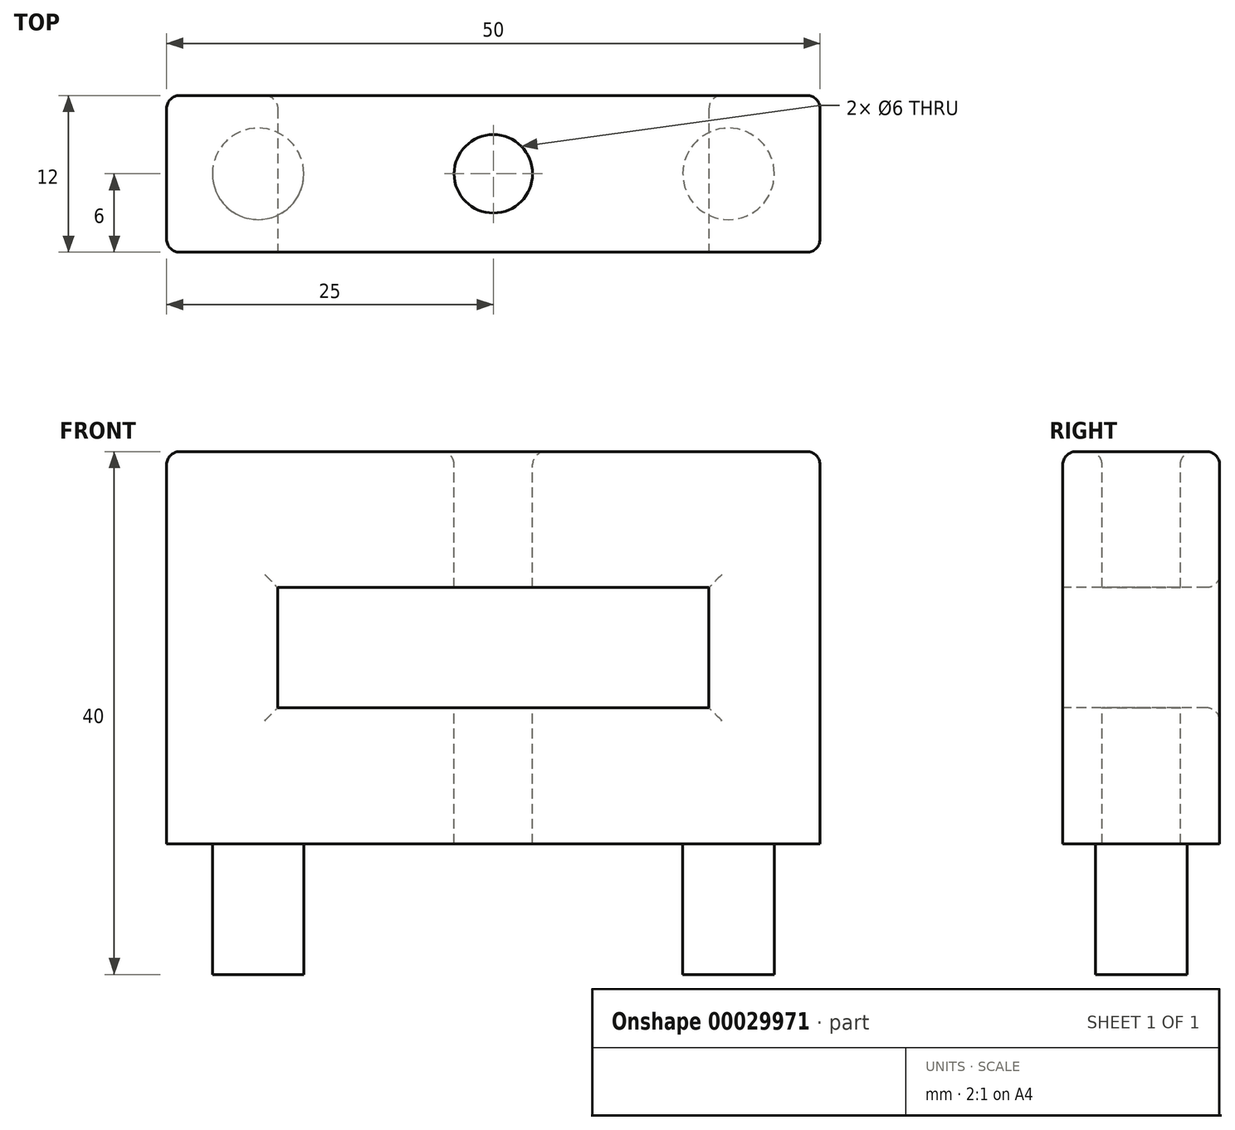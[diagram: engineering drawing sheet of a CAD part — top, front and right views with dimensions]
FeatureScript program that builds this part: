
annotation { "Feature Type Name" : "Feature", "Feature Type Description" : "" }
export const myFeature = defineFeature(function(context is Context, id is Id, definition is map)
    precondition{}
    {
        {
            var Q0;
            Q0=qCreatedBy(makeId("Top.planeOp"),FACE);
            var sketch = newSketch(context, id + "F0", { "sketchPlane" : qUnion([Q0])});
            skLineSegment(sketch, "E0.rect.bottom", {"start": v(25, -6) * mm, "end": v(-25, -6) * mm});
            skLineSegment(sketch, "E0.rect.top", {"start": v(25, 6) * mm, "end": v(-25, 6) * mm});
            skLineSegment(sketch, "E0.rect.left", {"start": v(25, -6) * mm, "end": v(25, 6) * mm});
            skLineSegment(sketch, "E0.rect.right", {"start": v(-25, -6) * mm, "end": v(-25, 6) * mm});
            skPoint(sketch, "E0.rect.middle", {"position": v(0, 0) * mm});
            skSolve(sketch);
        }
        {
            var Q0;
            Q0 = qSketchRegion(id + "F0", true);
            extrude(context, id + "F1", {"entities" : qUnion([Q0]), "depth" : 30 * mm});
        }
        {
            var Q0;
            Q0=makeQuery(id+"F1.opExtrude","CAP_FACE",FACE,{"disambiguationData":[OSD([sQuery(id+"F0.wireOp",EDGE,"E0.rect.bottom"),sQuery(id+"F0.wireOp",EDGE,"E0.rect.top"),sQuery(id+"F0.wireOp",EDGE,"E0.rect.left"),sQuery(id+"F0.wireOp",EDGE,"E0.rect.right")])],"isStart":false});
            var sketch = newSketch(context, id + "F2", { "sketchPlane" : qUnion([Q0])});
            skCircle(sketch, "E1", {"center": v(0, 0) * mm, "radius": 3 * mm});
            skSolve(sketch);
        }
        {
            var Q0;
            Q0 = qSketchRegion(id + "F2", true);
            extrude(context, id + "F3", {"entities" : qUnion([Q0]), "operationType" : NewBodyOperationType.REMOVE, "endBound" : BoundingType.THROUGH_ALL, "oppositeDirection" : true, "depth" : 25 * mm});
        }
        {
            var Q0;
            Q0=makeQuery(id+"F1.opExtrude","SWEPT_FACE",FACE,{"disambiguationData":[OSD([sQuery(id+"F0.wireOp",EDGE,"E0.rect.bottom")])]});
            var sketch = newSketch(context, id + "F4", { "sketchPlane" : qUnion([Q0])});
            skLineSegment(sketch, "E2.rect.bottom", {"start": v(16.5, 10.4) * mm, "end": v(-16.5, 10.4) * mm});
            skLineSegment(sketch, "E2.rect.top", {"start": v(16.5, 19.6) * mm, "end": v(-16.5, 19.6) * mm});
            skLineSegment(sketch, "E2.rect.left", {"start": v(16.5, 10.4) * mm, "end": v(16.5, 19.6) * mm});
            skLineSegment(sketch, "E2.rect.right", {"start": v(-16.5, 10.4) * mm, "end": v(-16.5, 19.6) * mm});
            skPoint(sketch, "E2.rect.middle", {"position": v(0, 15) * mm});
            skSolve(sketch);
        }
        {
            var Q0;
            Q0 = qSketchRegion(id + "F4", true);
            extrude(context, id + "F5", {"entities" : qUnion([Q0]), "operationType" : NewBodyOperationType.REMOVE, "endBound" : BoundingType.THROUGH_ALL, "oppositeDirection" : true, "depth" : 25 * mm});
        }
        {
            var Q0;
            Q0=makeQuery(id+"F1.opExtrude","SWEPT_EDGE",EDGE,{"disambiguationData":[OSD([sQuery(id+"F0.wireOp",EDGE,"E0.rect.bottom"),sQuery(id+"F0.wireOp",EDGE,"E0.rect.right")])]});
            var Q1;
            Q1=makeQuery(id+"F1.opExtrude","CAP_EDGE",EDGE,{"disambiguationData":[OSD([sQuery(id+"F0.wireOp",EDGE,"E0.rect.bottom")])],"isStart":false});
            var Q2;
            Q2=makeQuery(id+"F1.opExtrude","SWEPT_EDGE",EDGE,{"disambiguationData":[OSD([sQuery(id+"F0.wireOp",EDGE,"E0.rect.bottom"),sQuery(id+"F0.wireOp",EDGE,"E0.rect.left")])]});
            var Q3;
            Q3=makeQuery(id+"F1.opExtrude","SWEPT_EDGE",EDGE,{"disambiguationData":[OSD([sQuery(id+"F0.wireOp",EDGE,"E0.rect.top"),sQuery(id+"F0.wireOp",EDGE,"E0.rect.left")])]});
            var Q4;
            Q4=makeQuery(id+"F1.opExtrude","CAP_EDGE",EDGE,{"disambiguationData":[OSD([sQuery(id+"F0.wireOp",EDGE,"E0.rect.left")])],"isStart":false});
            var Q5;
            Q5=makeQuery(id+"F1.opExtrude","CAP_FACE",FACE,{"disambiguationData":[OSD([sQuery(id+"F0.wireOp",EDGE,"E0.rect.bottom"),sQuery(id+"F0.wireOp",EDGE,"E0.rect.top"),sQuery(id+"F0.wireOp",EDGE,"E0.rect.left"),sQuery(id+"F0.wireOp",EDGE,"E0.rect.right")])],"isStart":false});
            var Q6;
            Q6=makeQuery(id+"F1.opExtrude","CAP_EDGE",EDGE,{"disambiguationData":[OSD([sQuery(id+"F0.wireOp",EDGE,"E0.rect.top")])],"isStart":false});
            var Q7;
            Q7=makeQuery(id+"F1.opExtrude","SWEPT_EDGE",EDGE,{"disambiguationData":[OSD([sQuery(id+"F0.wireOp",EDGE,"E0.rect.top"),sQuery(id+"F0.wireOp",EDGE,"E0.rect.right")])]});
            var Q8;
            Q8=makeQuery(id+"F5.boolean.opBoolean","COPY",EDGE,{"derivedFrom":makeQuery(id+"F5.opExtrude","CAP_EDGE",EDGE,{"disambiguationData":[OSD([sQuery(id+"F4.wireOp",EDGE,"E2.rect.top")])],"isStart":true})});
            var Q9;
            Q9=makeQuery(id+"F5.boolean.opBoolean","COPY",EDGE,{"derivedFrom":makeQuery(id+"F5.opExtrude","CAP_EDGE",EDGE,{"disambiguationData":[OSD([sQuery(id+"F4.wireOp",EDGE,"E2.rect.right")])],"isStart":true})});
            var Q10;
            Q10=makeQuery(id+"F5.boolean.opBoolean","COPY",EDGE,{"derivedFrom":makeQuery(id+"F5.opExtrude","CAP_EDGE",EDGE,{"disambiguationData":[OSD([sQuery(id+"F4.wireOp",EDGE,"E2.rect.bottom")])],"isStart":true})});
            var Q11;
            Q11=makeQuery(id+"F5.boolean.opBoolean","COPY",EDGE,{"derivedFrom":makeQuery(id+"F5.opExtrude","CAP_EDGE",EDGE,{"disambiguationData":[OSD([sQuery(id+"F4.wireOp",EDGE,"E2.rect.left")])],"isStart":true})});
            var Q12;
            Q12=makeQuery(id+"F5.boolean.opBoolean","INTERSECT",EDGE,{"derivedFrom":[makeQuery(id+"F1.opExtrude","SWEPT_FACE",FACE,{"disambiguationData":[OSD([sQuery(id+"F0.wireOp",EDGE,"E0.rect.top")])]}),makeQuery(id+"F5.opExtrude","SWEPT_FACE",FACE,{"disambiguationData":[OSD([sQuery(id+"F4.wireOp",EDGE,"E2.rect.left")])]})]});
            var Q13;
            Q13=makeQuery(id+"F5.boolean.opBoolean","INTERSECT",EDGE,{"derivedFrom":[makeQuery(id+"F1.opExtrude","SWEPT_FACE",FACE,{"disambiguationData":[OSD([sQuery(id+"F0.wireOp",EDGE,"E0.rect.top")])]}),makeQuery(id+"F5.opExtrude","SWEPT_FACE",FACE,{"disambiguationData":[OSD([sQuery(id+"F4.wireOp",EDGE,"E2.rect.top")])]})]});
            var Q14;
            Q14=makeQuery(id+"F5.boolean.opBoolean","INTERSECT",EDGE,{"derivedFrom":[makeQuery(id+"F1.opExtrude","SWEPT_FACE",FACE,{"disambiguationData":[OSD([sQuery(id+"F0.wireOp",EDGE,"E0.rect.top")])]}),makeQuery(id+"F5.opExtrude","SWEPT_FACE",FACE,{"disambiguationData":[OSD([sQuery(id+"F4.wireOp",EDGE,"E2.rect.bottom")])]})]});
            var Q15;
            Q15=makeQuery(id+"F5.boolean.opBoolean","INTERSECT",EDGE,{"derivedFrom":[makeQuery(id+"F1.opExtrude","SWEPT_FACE",FACE,{"disambiguationData":[OSD([sQuery(id+"F0.wireOp",EDGE,"E0.rect.top")])]}),makeQuery(id+"F5.opExtrude","SWEPT_FACE",FACE,{"disambiguationData":[OSD([sQuery(id+"F4.wireOp",EDGE,"E2.rect.right")])]})]});
            fillet(context, id + "F6", {"entities" : qUnion([Q0, Q1, Q2, Q3, Q4, Q5, Q6, Q7, Q8, Q9, Q10, Q11, Q12, Q13, Q14, Q15]), "radius" : 1 * mm, "tangentPropagation" : true, "allowEdgeOverflow" : false});
        }
        {
            var Q0;
            Q0=makeQuery(id+"F1.opExtrude","CAP_FACE",FACE,{"disambiguationData":[OSD([sQuery(id+"F0.wireOp",EDGE,"E0.rect.bottom"),sQuery(id+"F0.wireOp",EDGE,"E0.rect.top"),sQuery(id+"F0.wireOp",EDGE,"E0.rect.left"),sQuery(id+"F0.wireOp",EDGE,"E0.rect.right")])],"isStart":true});
            var sketch = newSketch(context, id + "F7", { "sketchPlane" : qUnion([Q0])});
            skCircle(sketch, "E3", {"center": v(18, 0) * mm, "radius": 3.5 * mm});
            skCircle(sketch, "E4", {"center": v(-18, 0) * mm, "radius": 3.5 * mm});
            skSolve(sketch);
        }
        {
            var Q0;
            Q0 = qSketchRegion(id + "F7", true);
            extrude(context, id + "F8", {"entities" : qUnion([Q0]), "operationType" : NewBodyOperationType.ADD, "depth" : 10 * mm});
        }
    });
